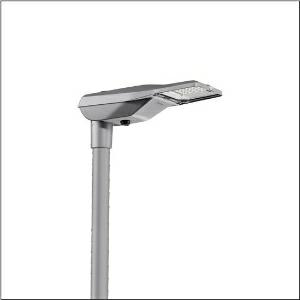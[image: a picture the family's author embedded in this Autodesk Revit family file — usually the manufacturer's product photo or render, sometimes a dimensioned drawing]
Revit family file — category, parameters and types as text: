
# Revit family: streetlight_sl_21_micro___p0_5a_5xe1v33r08db_e47d
name_source: partatom
category: Lighting Fixtures
units: mm (PartAtom-declared; Revit-internal decimal feet)

## family parameters
Cut with Voids When Loaded = No
Host = Face
Light Source = No
Part Type = Normal
Room Calculation Point = No
Round Connector Dimension = Use Diameter
Shared = No

## types (1)
- --- (1 x LED, 4940 lm, 39.1 W, 3000K)
    Apparent Load = 39 VA
    CIE Flux Codes = 37 73 96 100 100
    Color Rendering = 70
    Color Temperature = 3000K
    Default Elevation = 1800 mm
    Description = Streetlight SL 21 micro, mast luminaire, primary light control with lens, of PMMA, primary optical cover: cover, of toughened safety glass, transparent, light distribution: P0.5a, light emission: direct distribution, primary light characteristic: asymmetric, installation type: post-top, side-entry, LED, High Power LED, rated luminous flux: 4.940lm, luminous efficacy: 126lm/W, light colour: 730, colour temperature: 3000K, control gear: D4i, control: pre-setting: logarithmic dimming characteristic, flexible luminous flux parameterisation, time-dependent luminous flux control, constant luminous flux control, overheat protection, mains connection: 220..240V, AC, 50/60Hz, start of lifetime: 39W, end of service life: 41W, reduction: 18W, luminaire housing, of diecast aluminium, powder-coated, SITECO metallic grey (DB 702S), corrosivity category C5 high according to DIN EN ISO 12944, multi-level sealing system, sealing non-destructively replaceable, inclination adjustable: 0°, 5°, 10°, 15°, please order mast flange separately, length: 528mm, width: 235mm, height: 110mm, mast flange for spigot size: 42mm (side-entry): 5XC10008XM4, 60/48mm (side-entry/post-top): 5XC10108XM2, 76/60mm (side-entry/post-top): 5XC10108XM1, Smart Interface below, protection rating (complete): IP66, insulation class (complete): insulation class II (safety insulation), certification: CE, ENEC, ENEC+, VDE, impact resistance: IK10, permissible operating ambient temperature for outdoor applications: -40..+50°C, standard-compliant lighting for roads and squares, packaging unit: 1 piece

Light Distribution: P0.5a
    Height = 110 mm
    Lamp = 1 x LED
    Lamp Light Flux = 4940 lm
    Lamp Power = 39.1 W
    Lamp count = 1
    Length = 528 mm
    Luminous efficacy = 126 lm/W
    Manufacturer = Siteco
    ModVariant = No
    Model = 5XE1V33R08DB
    Number of Poles = 1
    OnlyDefault = Yes
    Power Factor = 1
    Product Name = Streetlight SL 21 micro | P0.5a
    Product group = mast luminaire | pylon top
    ProductGroupID = 6100
    Protection Class = Protection class II
    Protection Degree = IP 66
    RLX_Detail_Level = 1
    RLX_Emergency_Light_Flux = 0 lm
    RLX_Emergency_Type = 0
    RLX_Emergency_Type_DB = No
    RlxData = <blob elided: 98713 chars, md5=80d7037f>
    Socket = socket
    Standby Power = 0 W
    System Light Flux = 4940 lm
    System Power = 39 W
    Type Comments = factory setting: luminous flux: 100 % | dim-lin: 254 | 765 mA
    Type Image = l_1277290.jpg
    URL = http://relux.com
    VarID = @adj_077883
    Voltage = 0 V
    Weight = 0.00 kg
    Width = 235 mm

## geometry (parser evidence)
native form markers: Blend x4, Sweep x11
no freeform markers — native parametric forms only
